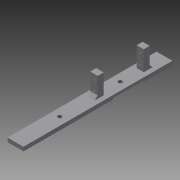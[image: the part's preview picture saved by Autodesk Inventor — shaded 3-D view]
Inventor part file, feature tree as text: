
AUTODESK INVENTOR PART (.ipt)
format: ipt  version: 2015 (Build 190159000, 159)  size: 142,848 bytes
history: native  units: in
note: dims shown in document units (in); Inventor stores cm internally (conversion verified against a paired STEP export)
features: extrude x5, sketch x5, reference x4, chamfer x2, fillet x1, projected_geometry x1
ambient origin geometry x8: Origin, YZ Plane, XZ Plane, XY Plane, X Axis, Y Axis, Z Axis, Center Point
bodies: Solid1 (feature_tree)
feature tree (18):
  extrude  "Extrusion1"  Depth=0.25in
  extrude  "Extrusion2"  Depth=0.25in
  extrude  "Extrusion3"  Depth=0.25in TaperAngle=0.0deg
  extrude  "Extrusion4"  Depth=2.075in TaperAngle=0.0deg
  chamfer  "Chamfer1"  Distance=0.375in
  extrude  "Extrusion5"  Depth=0.125in TaperAngle=0.0deg
  fillet  "Fillet1"  Radius=0.125in
  chamfer  "Chamfer2"  Distance=1.25in
  sketch  "Sketch1"  dims[d0=1.0in d1=0.25in]
  sketch  "Sketch2"  dims[d2=9.3625in d3=0.0in d6=0.25in]
  projected_geometry  "Projected Loop1"
  sketch  "Sketch3"  dims[d7=0.25in d8=4.8in d9=0.0in]
  sketch  "Sketch4"  dims[d10=3.8in d11=2.075in d12=0.0in]
  reference  "Reference1"
  reference  "Reference2"
  sketch  "Sketch5"  dims[d13=0.375in d14=0.375in d15=1.1875in d16=0.0in d17=0.1875in d18=0.125in d19=45.0deg d20=1.25in d21=0.0in d22=0.25in d23=0.1875in d24=0.125in d25=45.0deg]
  reference  "Reference3"
  reference  "Reference4"
